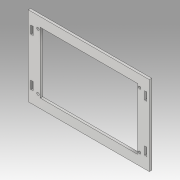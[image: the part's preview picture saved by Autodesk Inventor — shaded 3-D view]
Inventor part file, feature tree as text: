
AUTODESK INVENTOR PART (.ipt)
format: ipt  version: 2019.3 (Build 233278000, 278)  size: 131,072 bytes
history: native  units: mm
features: extrude x1
ambient origin geometry x8: Origin, YZ Plane, XZ Plane, XY Plane, X Axis, Y Axis, Z Axis, Center Point
bodies: Solid1 (feature_tree)
feature tree (1):
  extrude  "Extrusion1"  Depth=122.0mm
